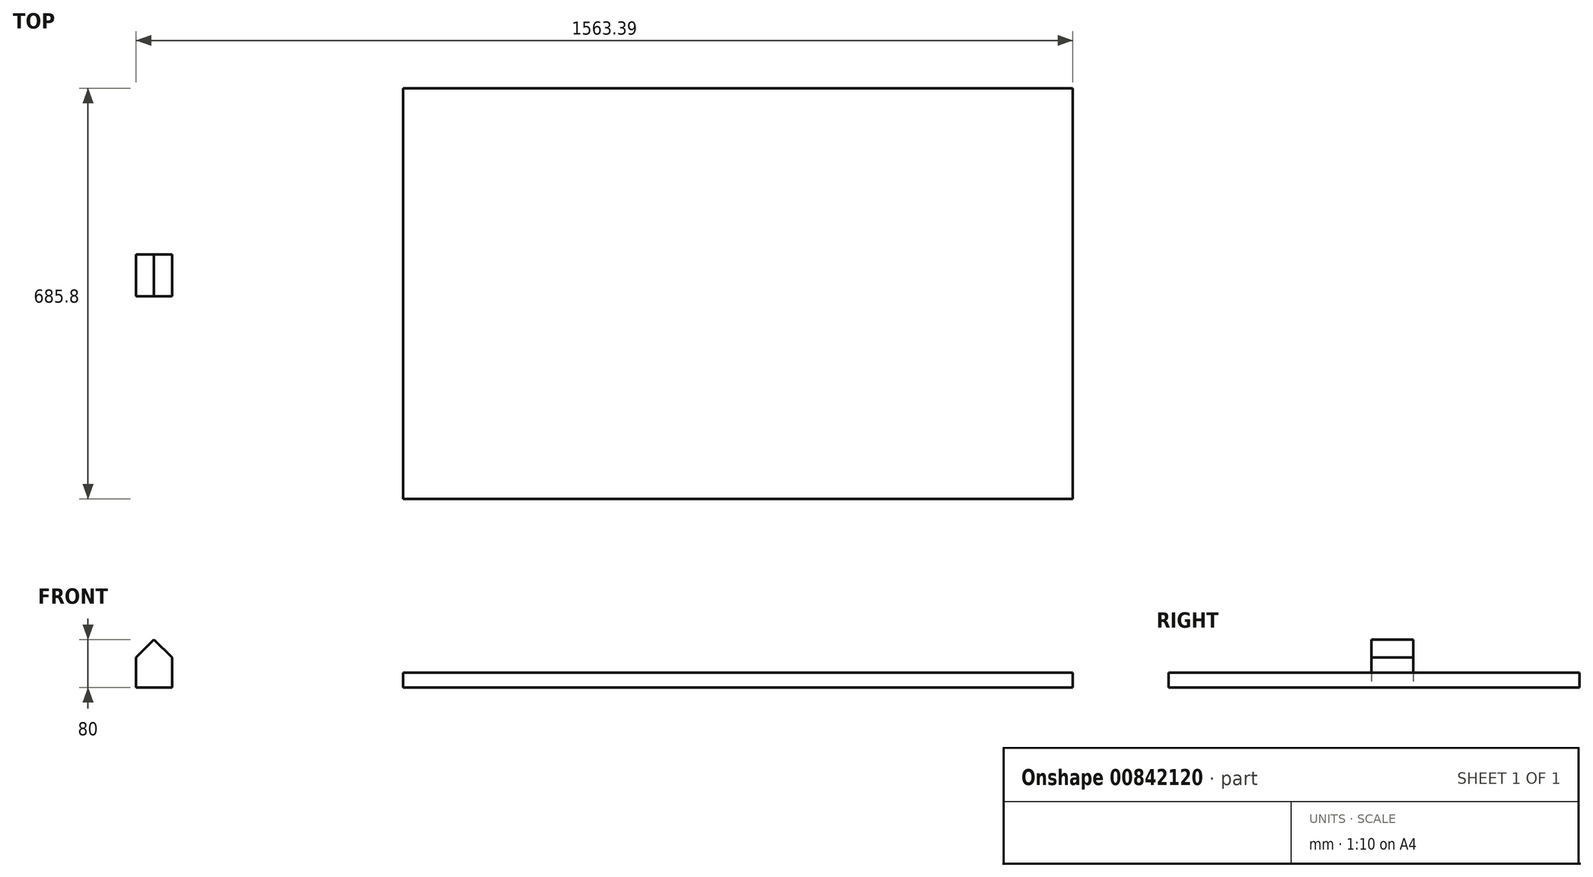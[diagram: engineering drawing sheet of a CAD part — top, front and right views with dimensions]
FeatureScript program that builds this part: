
annotation { "Feature Type Name" : "Feature", "Feature Type Description" : "" }
export const myFeature = defineFeature(function(context is Context, id is Id, definition is map)
    precondition{}
    {
        {
            var Q0;
            Q0=qCreatedBy(makeId("Top.planeOp"),FACE);
            var sketch = newSketch(context, id + "F0", { "sketchPlane" : qUnion([Q0])});
            skLineSegment(sketch, "E0.bottom", {"start": v(-574.79, 299.5) * mm, "end": v(542.81, 299.5) * mm});
            skLineSegment(sketch, "E0.top", {"start": v(-574.79, -386.3) * mm, "end": v(542.81, -386.3) * mm});
            skLineSegment(sketch, "E0.left", {"start": v(-574.79, 299.5) * mm, "end": v(-574.79, -386.3) * mm});
            skLineSegment(sketch, "E0.right", {"start": v(542.81, 299.5) * mm, "end": v(542.81, -386.3) * mm});
            skSolve(sketch);
        }
        {
            var Q0;
            Q0=makeQuery(id+"F0.imprint","IMPRINT",FACE,{"disambiguationData":[TD([[makeQuery(id+"F0.imprint","IMPRINT",EDGE,{"derivedFrom":sQuery(id+"F0.wireOp",EDGE,"E0.bottom")}),-1.0]])]});
            extrude(context, id + "F1", {"entities" : qUnion([Q0]), "depth" : 25 * mm, "offsetDistance" : 25 * mm});
        }
        {
            var Q0;
            Q0=qCreatedBy(makeId("Top.planeOp"),FACE);
            var sketch = newSketch(context, id + "F2", { "sketchPlane" : qUnion([Q0])});
            skLineSegment(sketch, "E1.bottom", {"start": v(-960.58, 22.06) * mm, "end": v(-1020.58, 22.06) * mm});
            skLineSegment(sketch, "E1.top", {"start": v(-960.58, -47.94) * mm, "end": v(-1020.58, -47.94) * mm});
            skLineSegment(sketch, "E1.left", {"start": v(-960.58, 22.06) * mm, "end": v(-960.58, -47.94) * mm});
            skLineSegment(sketch, "E1.right", {"start": v(-1020.58, 22.06) * mm, "end": v(-1020.58, -47.94) * mm});
            skSolve(sketch);
        }
        {
            var Q0;
            Q0=makeQuery(id+"F2.imprint","IMPRINT",FACE,{"disambiguationData":[TD([[makeQuery(id+"F2.imprint","IMPRINT",EDGE,{"derivedFrom":sQuery(id+"F2.wireOp",EDGE,"E1.bottom")}),1.0]])]});
            extrude(context, id + "F3", {"entities" : qUnion([Q0]), "depth" : 80 * mm, "offsetDistance" : 25 * mm});
        }
        {
            var Q0;
            Q0=makeQuery(id+"F3.opExtrude","CAP_EDGE",EDGE,{"disambiguationData":[OSD([sQuery(id+"F2.wireOp",EDGE,"E1.right")])],"isStart":false});
            var Q1;
            Q1=makeQuery(id+"F3.opExtrude","CAP_EDGE",EDGE,{"disambiguationData":[OSD([sQuery(id+"F2.wireOp",EDGE,"E1.left")])],"isStart":false});
            chamfer(context, id + "F4", {"entities" : qUnion([Q0, Q1]), "width" : 30 * mm, "tangentPropagation" : true});
        }
    });
